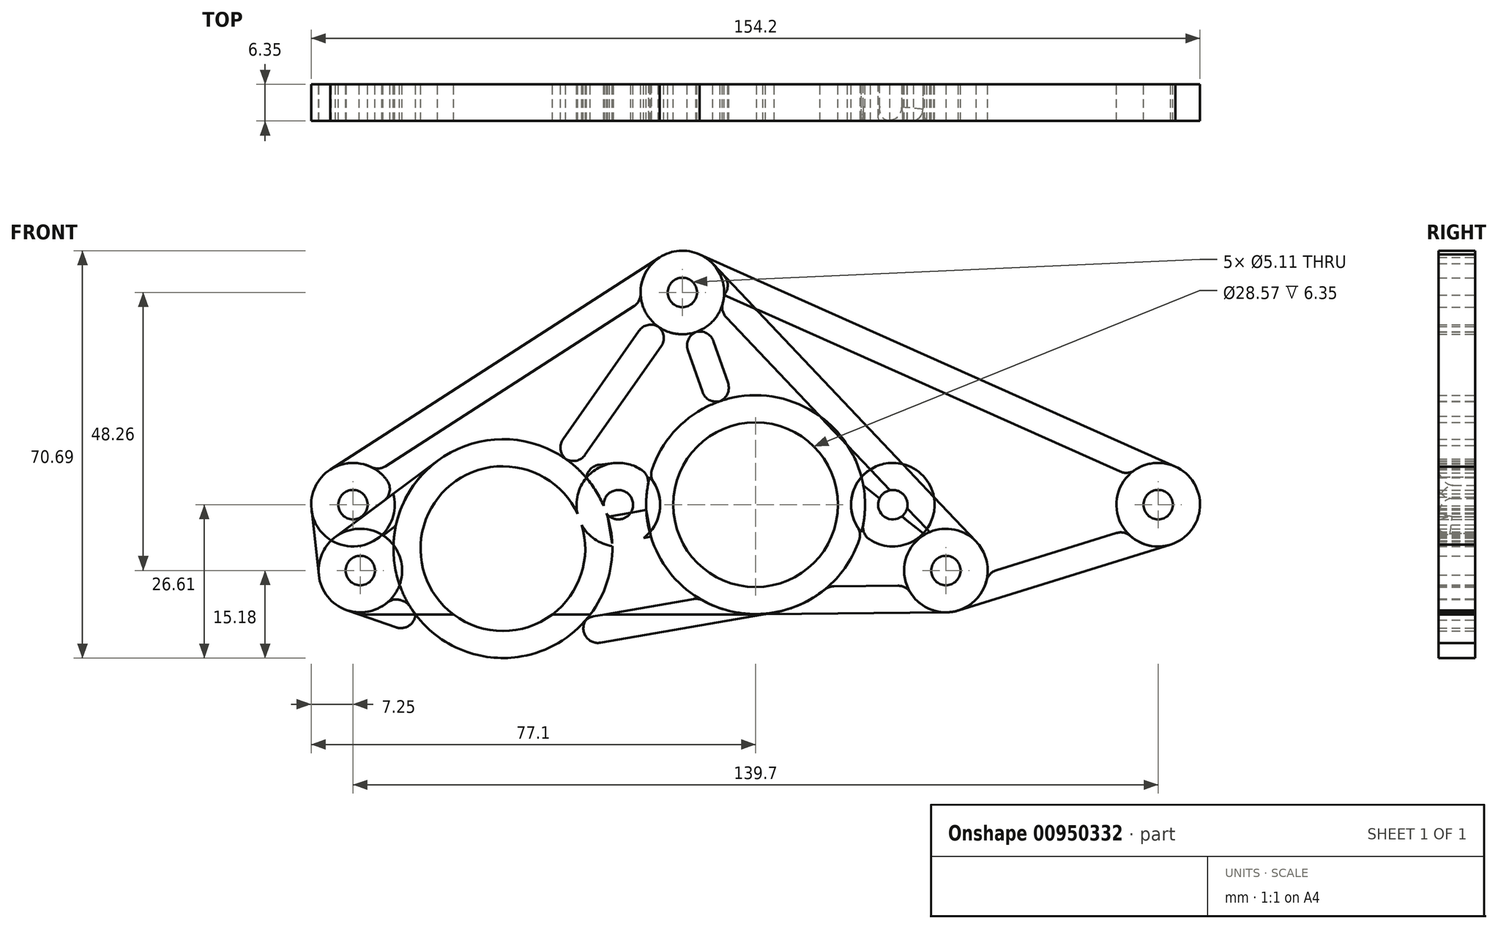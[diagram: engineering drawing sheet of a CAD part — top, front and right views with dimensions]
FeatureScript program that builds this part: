
annotation { "Feature Type Name" : "Feature", "Feature Type Description" : "" }
export const myFeature = defineFeature(function(context is Context, id is Id, definition is map)
    precondition{}
    {
        {
            var Q0;
            Q0=qCreatedBy(makeId("Front.planeOp"),FACE);
            var sketch = newSketch(context, id + "F0", { "sketchPlane" : qUnion([Q0])});
            skCircle(sketch, "E0", {"center": v(0, 0) * mm, "radius": 14.29 * mm});
            skCircle(sketch, "E1", {"center": v(-43.84, -7.62) * mm, "radius": 14.29 * mm});
            skCircle(sketch, "E2", {"center": v(-16.51, 54.1) * mm, "radius": 14.29 * mm, "construction": true});
            skCircle(sketch, "E3", {"center": v(18.98, 57.02) * mm, "radius": 6.35 * mm, "construction": true});
            skCircle(sketch, "E4", {"center": v(-50.18, 42.51) * mm, "radius": 6.35 * mm, "construction": true});
            skLineSegment(sketch, "E5.bottom", {"start": v(38.1, -19.05) * mm, "end": v(-76.2, -19.05) * mm});
            skLineSegment(sketch, "E5.top", {"start": v(38.1, 82.55) * mm, "end": v(-76.2, 82.55) * mm, "construction": true});
            skLineSegment(sketch, "E5.left", {"start": v(38.1, -19.05) * mm, "end": v(38.1, 82.55) * mm, "construction": true});
            skLineSegment(sketch, "E5.right", {"start": v(-76.2, -19.05) * mm, "end": v(-76.2, 82.55) * mm, "construction": true});
            skCircle(sketch, "E6", {"center": v(-68.58, -11.43) * mm, "radius": 2.55 * mm});
            skCircle(sketch, "E7", {"center": v(33.02, -11.43) * mm, "radius": 2.55 * mm});
            skCircle(sketch, "E8", {"center": v(-43.84, -7.62) * mm, "radius": 18.99 * mm});
            skCircle(sketch, "E9", {"center": v(0, 0) * mm, "radius": 18.99 * mm});
            skCircle(sketch, "E10", {"center": v(-12.7, 36.83) * mm, "radius": 2.55 * mm});
            skCircle(sketch, "E11", {"center": v(-12.7, 36.83) * mm, "radius": 7.25 * mm});
            skCircle(sketch, "E12", {"center": v(-68.58, -11.43) * mm, "radius": 7.25 * mm});
            skCircle(sketch, "E13", {"center": v(33.02, -11.43) * mm, "radius": 7.25 * mm});
            skLineSegment(sketch, "E14", {"start": v(11.88, 14.81) * mm, "end": v(37.56, -5.77) * mm, "construction": true});
            skLineSegment(sketch, "E15", {"start": v(0.18, -18.99) * mm, "end": v(33.09, -18.68) * mm});
            skLineSegment(sketch, "E16", {"start": v(18.7, 3.33) * mm, "end": v(29.32, -5.2) * mm});
            skLineSegment(sketch, "E17", {"start": v(12.64, -14.17) * mm, "end": v(26.26, -14.05) * mm});
            skLineSegment(sketch, "E18", {"start": v(-70.97, -18.28) * mm, "end": v(-50.09, -25.55) * mm});
            skLineSegment(sketch, "E19", {"start": v(-72.92, -5.62) * mm, "end": v(-55.2, 7.6) * mm});
            skLineSegment(sketch, "E20", {"start": v(-64.67, -5.33) * mm, "end": v(-62.4, -3.64) * mm});
            skLineSegment(sketch, "E21", {"start": v(-63, -16.07) * mm, "end": v(-60.35, -17) * mm});
            skLineSegment(sketch, "E22", {"start": v(-25.68, -2.08) * mm, "end": v(-18.96, -0.91) * mm});
            skLineSegment(sketch, "E23", {"start": v(-18.96, -0.91) * mm, "end": v(-18.16, -5.54) * mm});
            skLineSegment(sketch, "E24", {"start": v(-18.16, -5.54) * mm, "end": v(-24.88, -6.7) * mm});
            skLineSegment(sketch, "E25", {"start": v(-24.88, -6.7) * mm, "end": v(-25.68, -2.08) * mm});
            skLineSegment(sketch, "E26", {"start": v(-12.68, 29.58) * mm, "end": v(-8.36, 17.05) * mm});
            skLineSegment(sketch, "E27", {"start": v(-8.36, 17.05) * mm, "end": v(-3.92, 18.58) * mm, "construction": true});
            skLineSegment(sketch, "E28", {"start": v(-3.92, 18.58) * mm, "end": v(-8.24, 31.11) * mm});
            skLineSegment(sketch, "E29", {"start": v(-8.24, 31.11) * mm, "end": v(-12.68, 29.58) * mm, "construction": true});
            skLineSegment(sketch, "E30", {"start": v(-18.56, 32.56) * mm, "end": v(-34.96, 9.16) * mm});
            skLineSegment(sketch, "E31", {"start": v(-34.96, 9.16) * mm, "end": v(-31.1, 6.46) * mm, "construction": true});
            skLineSegment(sketch, "E32", {"start": v(-31.1, 6.46) * mm, "end": v(-14.71, 29.86) * mm});
            skLineSegment(sketch, "E33", {"start": v(-14.71, 29.86) * mm, "end": v(-18.56, 32.56) * mm, "construction": true});
            skCircle(sketch, "E34", {"center": v(0, 0) * mm, "radius": 23.81 * mm, "construction": true});
            skLineSegment(sketch, "E35", {"start": v(-7.44, 41.82) * mm, "end": v(38.28, -6.44) * mm});
            skLineSegment(sketch, "E36", {"start": v(-6.18, 33.66) * mm, "end": v(30.2, -4.75) * mm});
            skCircle(sketch, "E37", {"center": v(23.81, 0) * mm, "radius": 2.55 * mm});
            skCircle(sketch, "E38", {"center": v(23.81, 0) * mm, "radius": 7.25 * mm});
            skCircle(sketch, "E39", {"center": v(-23.81, 0) * mm, "radius": 2.55 * mm});
            skCircle(sketch, "E40", {"center": v(-23.81, 0) * mm, "radius": 7.25 * mm});
            skLineSegment(sketch, "E41", {"start": v(-69.85, 0) * mm, "end": v(69.85, 0) * mm, "construction": true});
            skCircle(sketch, "E42", {"center": v(69.85, 0) * mm, "radius": 2.55 * mm});
            skCircle(sketch, "E43", {"center": v(69.85, 0) * mm, "radius": 7.25 * mm});
            skCircle(sketch, "E44", {"center": v(-69.85, 0) * mm, "radius": 7.25 * mm});
            skCircle(sketch, "E45", {"center": v(-69.85, 0) * mm, "radius": 2.55 * mm});
            skLineSegment(sketch, "E46", {"start": v(-9.75, 43.45) * mm, "end": v(72.8, 6.62) * mm});
            skLineSegment(sketch, "E47", {"start": v(-5.46, 36.4) * mm, "end": v(64.7, 5.1) * mm});
            skLineSegment(sketch, "E48", {"start": v(64.12, -4.45) * mm, "end": v(40.26, -11.86) * mm});
            skLineSegment(sketch, "E49", {"start": v(72, -6.93) * mm, "end": v(35.17, -18.36) * mm});
            skLineSegment(sketch, "E50", {"start": v(-73.78, 6.1) * mm, "end": v(-16.63, 42.93) * mm});
            skLineSegment(sketch, "E51", {"start": v(-65.53, 5.82) * mm, "end": v(-19.79, 35.3) * mm});
            skLineSegment(sketch, "E52", {"start": v(-77.06, -0.8) * mm, "end": v(-75.79, -12.23) * mm});
            skLineSegment(sketch, "E53", {"start": v(-40.6, -26.33) * mm, "end": v(3.25, -18.7) * mm});
            skLineSegment(sketch, "E54", {"start": v(-29.08, -19.56) * mm, "end": v(-9.87, -16.22) * mm});
            skLineSegment(sketch, "E55", {"start": v(27.44, -6.28) * mm, "end": v(29.32, -5.2) * mm});
            skLineSegment(sketch, "E56", {"start": v(-31.1, 6.46) * mm, "end": v(-24.64, 7.2) * mm});
            skSolve(sketch);
        }
        {
            var Q0;
            Q0=makeQuery(id+"F0.imprint","IMPRINT",FACE,{"disambiguationData":[TD([[makeQuery(id+"F0.imprint","IMPRINT",EDGE,{"derivedFrom":sQuery(id+"F0.wireOp",EDGE,"E0")}),-1.0]])]});
            var Q1;
            {var subQ0=sQuery(id+"F0.wireOp",EDGE,"E5.bottom");var subQ1=sQuery(id+"F0.wireOp",EDGE,"E1");var subQ2=makeQuery(id+"F0.imprint","INTERSECT",VERTEX,{"disambiguationData":[OD(0.0)],"derivedFrom":[subQ1,subQ0]});Q1=makeQuery(id+"F0.imprint","IMPRINT",FACE,{"disambiguationData":[TD([[makeQuery(id+"F0.imprint","IMPRINT",EDGE,{"disambiguationData":[TD([[subQ2,-1.0]])],"derivedFrom":subQ1}),-1.0]])]});}
            var Q2;
            {var subQ0=sQuery(id+"F0.wireOp",EDGE,"E5.bottom");var subQ1=sQuery(id+"F0.wireOp",EDGE,"E1");var subQ2=makeQuery(id+"F0.imprint","INTERSECT",VERTEX,{"disambiguationData":[OD(0.0)],"derivedFrom":[subQ1,subQ0]});Q2=makeQuery(id+"F0.imprint","IMPRINT",FACE,{"disambiguationData":[TD([[makeQuery(id+"F0.imprint","IMPRINT",EDGE,{"disambiguationData":[TD([[subQ2,1.0]])],"derivedFrom":subQ1}),-1.0]])]});}
            var Q3;
            Q3=makeQuery(id+"F0.imprint","IMPRINT",FACE,{"disambiguationData":[TD([[makeQuery(id+"F0.imprint","IMPRINT",EDGE,{"derivedFrom":sQuery(id+"F0.wireOp",EDGE,"E7")}),-1.0]])]});
            var Q4;
            {var subQ0=sQuery(id+"F0.wireOp",EDGE,"E14");Q4=makeQuery(id+"F0.imprint","IMPRINT",FACE,{"disambiguationData":[TD([[makeQuery(id+"F0.imprint","IMPRINT",EDGE,{"derivedFrom":subQ0}),-1.0]])]});}
            var Q5;
            {var subQ0=sQuery(id+"F0.wireOp",EDGE,"E15");Q5=makeQuery(id+"F0.imprint","IMPRINT",FACE,{"disambiguationData":[TD([[makeQuery(id+"F0.imprint","IMPRINT",EDGE,{"derivedFrom":subQ0}),1.0]])]});}
            var Q6;
            {var subQ1=sQuery(id+"F0.wireOp",EDGE,"E22");Q6=makeQuery(id+"F0.imprint","IMPRINT",FACE,{"disambiguationData":[TD([[makeQuery(id+"F0.imprint","IMPRINT",EDGE,{"derivedFrom":subQ1}),-1.0]])]});}
            var Q7;
            {var subQ1=sQuery(id+"F0.wireOp",EDGE,"E26");Q7=makeQuery(id+"F0.imprint","IMPRINT",FACE,{"disambiguationData":[TD([[makeQuery(id+"F0.imprint","IMPRINT",EDGE,{"derivedFrom":subQ1}),1.0]])]});}
            var Q8;
            Q8=makeQuery(id+"F0.imprint","IMPRINT",FACE,{"disambiguationData":[TD([[makeQuery(id+"F0.imprint","IMPRINT",EDGE,{"derivedFrom":sQuery(id+"F0.wireOp",EDGE,"E10")}),-1.0]])]});
            var Q9;
            {var subQ1=sQuery(id+"F0.wireOp",EDGE,"E30");Q9=makeQuery(id+"F0.imprint","IMPRINT",FACE,{"disambiguationData":[TD([[makeQuery(id+"F0.imprint","IMPRINT",EDGE,{"derivedFrom":subQ1}),1.0]])]});}
            var Q10;
            {var subQ0=sQuery(id+"F0.wireOp",EDGE,"E33");Q10=makeQuery(id+"F0.imprint","IMPRINT",FACE,{"disambiguationData":[TD([[makeQuery(id+"F0.imprint","IMPRINT",EDGE,{"derivedFrom":subQ0}),1.0]])]});}
            var Q11;
            {var subQ0=sQuery(id+"F0.wireOp",EDGE,"E29");Q11=makeQuery(id+"F0.imprint","IMPRINT",FACE,{"disambiguationData":[TD([[makeQuery(id+"F0.imprint","IMPRINT",EDGE,{"derivedFrom":subQ0}),1.0]])]});}
            var Q12;
            {var subQ0=sQuery(id+"F0.wireOp",EDGE,"E27");Q12=makeQuery(id+"F0.imprint","IMPRINT",FACE,{"disambiguationData":[TD([[makeQuery(id+"F0.imprint","IMPRINT",EDGE,{"derivedFrom":subQ0}),1.0]])]});}
            var Q13;
            {var subQ0=sQuery(id+"F0.wireOp",EDGE,"E23");Q13=makeQuery(id+"F0.imprint","IMPRINT",FACE,{"disambiguationData":[TD([[makeQuery(id+"F0.imprint","IMPRINT",EDGE,{"derivedFrom":subQ0}),-1.0]])]});}
            var Q14;
            {var subQ0=sQuery(id+"F0.wireOp",EDGE,"E25");Q14=makeQuery(id+"F0.imprint","IMPRINT",FACE,{"disambiguationData":[TD([[makeQuery(id+"F0.imprint","IMPRINT",EDGE,{"derivedFrom":subQ0}),-1.0]])]});}
            var Q15;
            {var subQ5=sQuery(id+"F0.wireOp",EDGE,"E21");Q15=makeQuery(id+"F0.imprint","IMPRINT",FACE,{"disambiguationData":[TD([[makeQuery(id+"F0.imprint","IMPRINT",EDGE,{"derivedFrom":subQ5}),-1.0]])]});}
            var Q16;
            {var subQ0=sQuery(id+"F0.wireOp",EDGE,"E19");Q16=makeQuery(id+"F0.imprint","IMPRINT",FACE,{"disambiguationData":[TD([[makeQuery(id+"F0.imprint","IMPRINT",EDGE,{"derivedFrom":subQ0}),-1.0]])]});}
            var Q17;
            Q17=makeQuery(id+"F0.imprint","IMPRINT",FACE,{"disambiguationData":[TD([[makeQuery(id+"F0.imprint","IMPRINT",EDGE,{"derivedFrom":sQuery(id+"F0.wireOp",EDGE,"E6")}),-1.0]])]});
            var Q18;
            {var subQ0=sQuery(id+"F0.wireOp",EDGE,"E18");var subQ1=sQuery(id+"F0.wireOp",EDGE,"E5.bottom");var subQ2=makeQuery(id+"F0.imprint","INTERSECT",VERTEX,{"derivedFrom":[subQ1,subQ0]});Q18=makeQuery(id+"F0.imprint","IMPRINT",FACE,{"disambiguationData":[TD([[makeQuery(id+"F0.imprint","IMPRINT",EDGE,{"disambiguationData":[TD([[subQ2,1.0]])],"derivedFrom":subQ1}),1.0]])]});}
            var Q19;
            {var subQ0=sQuery(id+"F0.wireOp",EDGE,"E31");Q19=makeQuery(id+"F0.imprint","IMPRINT",FACE,{"disambiguationData":[TD([[makeQuery(id+"F0.imprint","IMPRINT",EDGE,{"derivedFrom":subQ0}),1.0]])]});}
            var Q20;
            {var subQ0=sQuery(id+"F0.wireOp",EDGE,"E13");var subQ1=sQuery(id+"F0.wireOp",EDGE,"E5.left");var subQ2=makeQuery(id+"F0.imprint","INTERSECT",VERTEX,{"disambiguationData":[OD(0.0)],"derivedFrom":[subQ1,subQ0]});Q20=makeQuery(id+"F0.imprint","IMPRINT",FACE,{"disambiguationData":[TD([[makeQuery(id+"F0.imprint","IMPRINT",EDGE,{"disambiguationData":[TD([[subQ2,-1.0]])],"derivedFrom":subQ1}),-1.0]])]});}
            var Q21;
            {var subQ5=sQuery(id+"F0.wireOp",EDGE,"E25");Q21=makeQuery(id+"F0.imprint","IMPRINT",FACE,{"disambiguationData":[TD([[makeQuery(id+"F0.imprint","IMPRINT",EDGE,{"derivedFrom":subQ5}),1.0]])]});}
            var Q22;
            {var subQ1=sQuery(id+"F0.wireOp",EDGE,"E9");var subQ3=sQuery(id+"F0.wireOp",EDGE,"E40");var subQ4=makeQuery(id+"F0.imprint","INTERSECT",VERTEX,{"disambiguationData":[OD(0.0)],"derivedFrom":[subQ1,subQ3]});Q22=makeQuery(id+"F0.imprint","IMPRINT",FACE,{"disambiguationData":[TD([[makeQuery(id+"F0.imprint","IMPRINT",EDGE,{"disambiguationData":[TD([[subQ4,1.0]])],"derivedFrom":subQ3}),1.0]])]});}
            var Q23;
            {var subQ0=sQuery(id+"F0.wireOp",EDGE,"E22");Q23=makeQuery(id+"F0.imprint","IMPRINT",FACE,{"disambiguationData":[TD([[makeQuery(id+"F0.imprint","IMPRINT",EDGE,{"derivedFrom":subQ0}),1.0]])]});}
            var Q24;
            {var subQ5=sQuery(id+"F0.wireOp",EDGE,"E36");var subQ7=sQuery(id+"F0.wireOp",EDGE,"E9");var subQ9=makeQuery(id+"F0.imprint","INTERSECT",VERTEX,{"disambiguationData":[OD(0.0)],"derivedFrom":[subQ7,subQ5]});Q24=makeQuery(id+"F0.imprint","IMPRINT",FACE,{"disambiguationData":[TD([[makeQuery(id+"F0.imprint","IMPRINT",EDGE,{"disambiguationData":[TD([[subQ9,-1.0]])],"derivedFrom":subQ7}),-1.0]])]});}
            var Q25;
            {var subQ0=sQuery(id+"F0.wireOp",EDGE,"E36");var subQ1=sQuery(id+"F0.wireOp",EDGE,"E9");var subQ2=makeQuery(id+"F0.imprint","INTERSECT",VERTEX,{"disambiguationData":[OD(0.0)],"derivedFrom":[subQ1,subQ0]});Q25=makeQuery(id+"F0.imprint","IMPRINT",FACE,{"disambiguationData":[TD([[makeQuery(id+"F0.imprint","IMPRINT",EDGE,{"disambiguationData":[TD([[subQ2,-1.0]])],"derivedFrom":subQ1}),1.0]])]});}
            var Q26;
            {var subQ0=sQuery(id+"F0.wireOp",EDGE,"E9");var subQ1=makeQuery(id+"F0.imprint","INTERSECT",VERTEX,{"derivedFrom":[subQ0,sQuery(id+"F0.wireOp",EDGE,"E16")]});Q26=makeQuery(id+"F0.imprint","IMPRINT",FACE,{"disambiguationData":[TD([[makeQuery(id+"F0.imprint","IMPRINT",EDGE,{"disambiguationData":[TD([[subQ1,-1.0]])],"derivedFrom":subQ0}),1.0]])]});}
            var Q27;
            {var subQ0=sQuery(id+"F0.wireOp",EDGE,"E37");var subQ1=sQuery(id+"F0.wireOp",EDGE,"E16");var subQ2=makeQuery(id+"F0.imprint","INTERSECT",VERTEX,{"disambiguationData":[OD(1.0)],"derivedFrom":[subQ1,subQ0]});Q27=makeQuery(id+"F0.imprint","IMPRINT",FACE,{"disambiguationData":[TD([[makeQuery(id+"F0.imprint","IMPRINT",EDGE,{"disambiguationData":[TD([[subQ2,-1.0]])],"derivedFrom":subQ1}),1.0]])]});}
            var Q28;
            {var subQ4=sQuery(id+"F0.wireOp",EDGE,"E38");var subQ7=sQuery(id+"F0.wireOp",EDGE,"E35");var subQ8=makeQuery(id+"F0.imprint","INTERSECT",VERTEX,{"disambiguationData":[OD(0.0)],"derivedFrom":[subQ7,subQ4]});Q28=makeQuery(id+"F0.imprint","IMPRINT",FACE,{"disambiguationData":[TD([[makeQuery(id+"F0.imprint","IMPRINT",EDGE,{"disambiguationData":[TD([[subQ8,-1.0]])],"derivedFrom":subQ7}),-1.0]])]});}
            var Q29;
            {var subQ0=sQuery(id+"F0.wireOp",EDGE,"E38");var subQ1=sQuery(id+"F0.wireOp",EDGE,"E35");var subQ2=makeQuery(id+"F0.imprint","INTERSECT",VERTEX,{"disambiguationData":[OD(0.0)],"derivedFrom":[subQ1,subQ0]});Q29=makeQuery(id+"F0.imprint","IMPRINT",FACE,{"disambiguationData":[TD([[makeQuery(id+"F0.imprint","IMPRINT",EDGE,{"disambiguationData":[TD([[subQ2,-1.0]])],"derivedFrom":subQ1}),1.0]])]});}
            var Q30;
            {var subQ0=sQuery(id+"F0.wireOp",EDGE,"E35");var subQ1=sQuery(id+"F0.wireOp",EDGE,"E13");var subQ2=makeQuery(id+"F0.imprint","INTERSECT",VERTEX,{"derivedFrom":[subQ1,subQ0]});Q30=makeQuery(id+"F0.imprint","IMPRINT",FACE,{"disambiguationData":[TD([[makeQuery(id+"F0.imprint","IMPRINT",EDGE,{"disambiguationData":[TD([[subQ2,-1.0]])],"derivedFrom":subQ1}),-1.0]])]});}
            var Q31;
            {var subQ0=sQuery(id+"F0.wireOp",EDGE,"E16");var subQ1=sQuery(id+"F0.wireOp",EDGE,"E13");var subQ2=makeQuery(id+"F0.imprint","INTERSECT",VERTEX,{"derivedFrom":[subQ1,subQ0]});Q31=makeQuery(id+"F0.imprint","IMPRINT",FACE,{"disambiguationData":[TD([[makeQuery(id+"F0.imprint","IMPRINT",EDGE,{"disambiguationData":[TD([[subQ2,1.0]])],"derivedFrom":subQ1}),-1.0]])]});}
            var Q32;
            {var subQ1=sQuery(id+"F0.wireOp",EDGE,"E16");var subQ7=sQuery(id+"F0.wireOp",EDGE,"E9");var subQ8=makeQuery(id+"F0.imprint","INTERSECT",VERTEX,{"derivedFrom":[subQ7,subQ1]});Q32=makeQuery(id+"F0.imprint","IMPRINT",FACE,{"disambiguationData":[TD([[makeQuery(id+"F0.imprint","IMPRINT",EDGE,{"disambiguationData":[TD([[subQ8,-1.0]])],"derivedFrom":subQ7}),-1.0]])]});}
            var Q33;
            {var subQ1=sQuery(id+"F0.wireOp",EDGE,"E16");var subQ6=sQuery(id+"F0.wireOp",EDGE,"E9");var subQ7=makeQuery(id+"F0.imprint","INTERSECT",VERTEX,{"derivedFrom":[subQ6,subQ1]});Q33=makeQuery(id+"F0.imprint","IMPRINT",FACE,{"disambiguationData":[TD([[makeQuery(id+"F0.imprint","IMPRINT",EDGE,{"disambiguationData":[TD([[subQ7,1.0]])],"derivedFrom":subQ6}),-1.0]])]});}
            var Q34;
            {var subQ0=sQuery(id+"F0.wireOp",EDGE,"E40");var subQ1=sQuery(id+"F0.wireOp",EDGE,"E1");var subQ2=makeQuery(id+"F0.imprint","INTERSECT",VERTEX,{"disambiguationData":[OD(1.0)],"derivedFrom":[subQ1,subQ0]});Q34=makeQuery(id+"F0.imprint","IMPRINT",FACE,{"disambiguationData":[TD([[makeQuery(id+"F0.imprint","IMPRINT",EDGE,{"disambiguationData":[TD([[subQ2,1.0]])],"derivedFrom":subQ1}),-1.0]])]});}
            var Q35;
            {var subQ0=sQuery(id+"F0.wireOp",EDGE,"E46");Q35=makeQuery(id+"F0.imprint","IMPRINT",FACE,{"disambiguationData":[TD([[makeQuery(id+"F0.imprint","IMPRINT",EDGE,{"derivedFrom":subQ0}),-1.0]])]});}
            var Q36;
            Q36=makeQuery(id+"F0.imprint","IMPRINT",FACE,{"disambiguationData":[TD([[makeQuery(id+"F0.imprint","IMPRINT",EDGE,{"derivedFrom":sQuery(id+"F0.wireOp",EDGE,"E42")}),-1.0]])]});
            var Q37;
            {var subQ0=sQuery(id+"F0.wireOp",EDGE,"E48");Q37=makeQuery(id+"F0.imprint","IMPRINT",FACE,{"disambiguationData":[TD([[makeQuery(id+"F0.imprint","IMPRINT",EDGE,{"derivedFrom":subQ0}),1.0]])]});}
            var Q38;
            {var subQ0=sQuery(id+"F0.wireOp",EDGE,"E35");var subQ1=sQuery(id+"F0.wireOp",EDGE,"E11");var subQ2=makeQuery(id+"F0.imprint","INTERSECT",VERTEX,{"derivedFrom":[subQ1,subQ0]});Q38=makeQuery(id+"F0.imprint","IMPRINT",FACE,{"disambiguationData":[TD([[makeQuery(id+"F0.imprint","IMPRINT",EDGE,{"disambiguationData":[TD([[subQ2,1.0]])],"derivedFrom":subQ1}),-1.0]])]});}
            var Q39;
            Q39=makeQuery(id+"F0.imprint","IMPRINT",FACE,{"disambiguationData":[TD([[makeQuery(id+"F0.imprint","IMPRINT",EDGE,{"derivedFrom":sQuery(id+"F0.wireOp",EDGE,"E45")}),-1.0]])]});
            var Q40;
            {var subQ0=sQuery(id+"F0.wireOp",EDGE,"E12");var subQ1=makeQuery(id+"F0.imprint","INTERSECT",VERTEX,{"derivedFrom":[subQ0,sQuery(id+"F0.wireOp",EDGE,"E19")]});Q40=makeQuery(id+"F0.imprint","IMPRINT",FACE,{"disambiguationData":[TD([[makeQuery(id+"F0.imprint","IMPRINT",EDGE,{"disambiguationData":[TD([[subQ1,1.0]])],"derivedFrom":subQ0}),1.0]])]});}
            var Q41;
            {var subQ0=sQuery(id+"F0.wireOp",EDGE,"E20");Q41=makeQuery(id+"F0.imprint","IMPRINT",FACE,{"disambiguationData":[TD([[makeQuery(id+"F0.imprint","IMPRINT",EDGE,{"derivedFrom":subQ0}),1.0]])]});}
            var Q42;
            {var subQ0=sQuery(id+"F0.wireOp",EDGE,"E50");Q42=makeQuery(id+"F0.imprint","IMPRINT",FACE,{"disambiguationData":[TD([[makeQuery(id+"F0.imprint","IMPRINT",EDGE,{"derivedFrom":subQ0}),-1.0]])]});}
            var Q43;
            {var subQ0=sQuery(id+"F0.wireOp",EDGE,"E53");var subQ1=sQuery(id+"F0.wireOp",EDGE,"E5.bottom");var subQ2=makeQuery(id+"F0.imprint","INTERSECT",VERTEX,{"derivedFrom":[subQ1,subQ0]});Q43=makeQuery(id+"F0.imprint","IMPRINT",FACE,{"disambiguationData":[TD([[makeQuery(id+"F0.imprint","IMPRINT",EDGE,{"disambiguationData":[TD([[subQ2,-1.0]])],"derivedFrom":subQ1}),1.0]])]});}
            var Q44;
            {var subQ3=sQuery(id+"F0.wireOp",EDGE,"E53");var subQ7=sQuery(id+"F0.wireOp",EDGE,"E5.bottom");var subQ8=makeQuery(id+"F0.imprint","INTERSECT",VERTEX,{"derivedFrom":[subQ7,subQ3]});Q44=makeQuery(id+"F0.imprint","IMPRINT",FACE,{"disambiguationData":[TD([[makeQuery(id+"F0.imprint","IMPRINT",EDGE,{"disambiguationData":[TD([[subQ8,-1.0]])],"derivedFrom":subQ7}),-1.0]])]});}
            var Q45;
            {var subQ0=sQuery(id+"F0.wireOp",EDGE,"E17");Q45=makeQuery(id+"F0.imprint","IMPRINT",FACE,{"disambiguationData":[TD([[makeQuery(id+"F0.imprint","IMPRINT",EDGE,{"derivedFrom":subQ0}),-1.0]])]});}
            var Q46;
            {var subQ0=sQuery(id+"F0.wireOp",EDGE,"E52");Q46=makeQuery(id+"F0.imprint","IMPRINT",FACE,{"disambiguationData":[TD([[makeQuery(id+"F0.imprint","IMPRINT",EDGE,{"derivedFrom":subQ0}),1.0]])]});}
            var Q47;
            {var subQ0=sQuery(id+"F0.wireOp",EDGE,"E55");Q47=makeQuery(id+"F0.imprint","IMPRINT",FACE,{"disambiguationData":[TD([[makeQuery(id+"F0.imprint","IMPRINT",EDGE,{"derivedFrom":subQ0}),1.0]])]});}
            var Q48;
            {var subQ0=sQuery(id+"F0.wireOp",EDGE,"E56");Q48=makeQuery(id+"F0.imprint","IMPRINT",FACE,{"disambiguationData":[TD([[makeQuery(id+"F0.imprint","IMPRINT",EDGE,{"derivedFrom":subQ0}),-1.0]])]});}
            var Q49;
            {var subQ0=sQuery(id+"F0.wireOp",EDGE,"E38");var subQ1=sQuery(id+"F0.wireOp",EDGE,"E9");var subQ2=makeQuery(id+"F0.imprint","INTERSECT",VERTEX,{"disambiguationData":[OD(0.0)],"derivedFrom":[subQ1,subQ0]});Q49=makeQuery(id+"F0.imprint","IMPRINT",FACE,{"disambiguationData":[TD([[makeQuery(id+"F0.imprint","IMPRINT",EDGE,{"disambiguationData":[TD([[subQ2,-1.0]])],"derivedFrom":subQ1}),-1.0]])]});}
            var Q50;
            {var subQ0=sQuery(id+"F0.wireOp",EDGE,"E12");var subQ1=sQuery(id+"F0.wireOp",EDGE,"E8");var subQ2=makeQuery(id+"F0.imprint","INTERSECT",VERTEX,{"disambiguationData":[OD(0.0)],"derivedFrom":[subQ1,subQ0]});Q50=makeQuery(id+"F0.imprint","IMPRINT",FACE,{"disambiguationData":[TD([[makeQuery(id+"F0.imprint","IMPRINT",EDGE,{"disambiguationData":[TD([[subQ2,-1.0]])],"derivedFrom":subQ1}),1.0]])]});}
            var Q51;
            {var subQ0=sQuery(id+"F0.wireOp",EDGE,"E39");var subQ1=sQuery(id+"F0.wireOp",EDGE,"E8");var subQ2=makeQuery(id+"F0.imprint","INTERSECT",VERTEX,{"disambiguationData":[OD(1.0)],"derivedFrom":[subQ1,subQ0]});Q51=makeQuery(id+"F0.imprint","IMPRINT",FACE,{"disambiguationData":[TD([[makeQuery(id+"F0.imprint","IMPRINT",EDGE,{"disambiguationData":[TD([[subQ2,-1.0]])],"derivedFrom":subQ1}),-1.0]])]});}
            var Q52;
            {var subQ1=sQuery(id+"F0.wireOp",EDGE,"E9");var subQ3=sQuery(id+"F0.wireOp",EDGE,"E40");var subQ4=makeQuery(id+"F0.imprint","INTERSECT",VERTEX,{"disambiguationData":[OD(1.0)],"derivedFrom":[subQ1,subQ3]});Q52=makeQuery(id+"F0.imprint","IMPRINT",FACE,{"disambiguationData":[TD([[makeQuery(id+"F0.imprint","IMPRINT",EDGE,{"disambiguationData":[TD([[subQ4,1.0]])],"derivedFrom":subQ3}),-1.0]])]});}
            extrude(context, id + "F1", {"entities" : qUnion([Q0, Q1, Q2, Q3, Q4, Q5, Q6, Q7, Q8, Q9, Q10, Q11, Q12, Q13, Q14, Q15, Q16, Q17, Q18, Q19, Q20, Q21, Q22, Q23, Q24, Q25, Q26, Q27, Q28, Q29, Q30, Q31, Q32, Q33, Q34, Q35, Q36, Q37, Q38, Q39, Q40, Q41, Q42, Q43, Q44, Q45, Q46, Q47, Q48, Q49, Q50, Q51, Q52]), "depth" : 6.35 * mm, "offsetDistance" : 25.4 * mm});
        }
        {
            var Q0;
            Q0=makeQuery(id+"F1.opExtrude","SWEPT_EDGE",EDGE,{"disambiguationData":[OSD([sQuery(id+"F0.wireOp",EDGE,"E12"),sQuery(id+"F0.wireOp",EDGE,"E20")])]});
            var Q1;
            Q1=makeQuery(id+"F1.opExtrude","SWEPT_EDGE",EDGE,{"disambiguationData":[OSD([sQuery(id+"F0.wireOp",EDGE,"E12"),sQuery(id+"F0.wireOp",EDGE,"E21")])]});
            var Q2;
            Q2=makeQuery(id+"F1.opExtrude","SWEPT_EDGE",EDGE,{"disambiguationData":[OSD([sQuery(id+"F0.wireOp",EDGE,"E8"),sQuery(id+"F0.wireOp",EDGE,"E21")])]});
            var Q3;
            Q3=makeQuery(id+"F1.opExtrude","SWEPT_EDGE",EDGE,{"disambiguationData":[OSD([sQuery(id+"F0.wireOp",EDGE,"E44"),sQuery(id+"F0.wireOp",EDGE,"E51")])]});
            var Q4;
            Q4=makeQuery(id+"F1.opExtrude","SWEPT_EDGE",EDGE,{"disambiguationData":[OSD([sQuery(id+"F0.wireOp",EDGE,"E19"),sQuery(id+"F0.wireOp",EDGE,"E44")])]});
            var Q5;
            Q5=makeQuery(id+"F1.opExtrude","SWEPT_EDGE",EDGE,{"disambiguationData":[OSD([sQuery(id+"F0.wireOp",EDGE,"E8"),sQuery(id+"F0.wireOp",EDGE,"E30")])]});
            var Q6;
            Q6=makeQuery(id+"F1.opExtrude","SWEPT_EDGE",EDGE,{"disambiguationData":[OSD([sQuery(id+"F0.wireOp",EDGE,"E11"),sQuery(id+"F0.wireOp",EDGE,"E51")])]});
            var Q7;
            Q7=makeQuery(id+"F1.opExtrude","SWEPT_EDGE",EDGE,{"disambiguationData":[OSD([sQuery(id+"F0.wireOp",EDGE,"E11"),sQuery(id+"F0.wireOp",EDGE,"E30")])]});
            var Q8;
            Q8=makeQuery(id+"F1.opExtrude","SWEPT_EDGE",EDGE,{"disambiguationData":[OSD([sQuery(id+"F0.wireOp",EDGE,"E11"),sQuery(id+"F0.wireOp",EDGE,"E32")])]});
            var Q9;
            Q9=makeQuery(id+"F1.opExtrude","SWEPT_EDGE",EDGE,{"disambiguationData":[OSD([sQuery(id+"F0.wireOp",EDGE,"E11"),sQuery(id+"F0.wireOp",EDGE,"E26")])]});
            var Q10;
            {var subQ0=sQuery(id+"F0.wireOp",EDGE,"E40");var subQ1=sQuery(id+"F0.wireOp",EDGE,"E9");Q10=makeQuery(id+"F1.opExtrude","SWEPT_EDGE",EDGE,{"disambiguationData":[OSD([subQ1,subQ0]),TDD([makeQuery(id+"F0.imprint","INTERSECT",VERTEX,{"disambiguationData":[OD(0.0)],"derivedFrom":[subQ1,subQ0]})])]});}
            var Q11;
            Q11=makeQuery(id+"F1.opExtrude","SWEPT_EDGE",EDGE,{"disambiguationData":[OSD([sQuery(id+"F0.wireOp",EDGE,"E9"),sQuery(id+"F0.wireOp",EDGE,"E26")])]});
            var Q12;
            Q12=makeQuery(id+"F1.opExtrude","SWEPT_EDGE",EDGE,{"disambiguationData":[OSD([sQuery(id+"F0.wireOp",EDGE,"E9"),sQuery(id+"F0.wireOp",EDGE,"E28")])]});
            var Q13;
            Q13=makeQuery(id+"F1.opExtrude","SWEPT_EDGE",EDGE,{"disambiguationData":[OSD([sQuery(id+"F0.wireOp",EDGE,"E8"),sQuery(id+"F0.wireOp",EDGE,"E54")])]});
            var Q14;
            Q14=makeQuery(id+"F1.opExtrude","SWEPT_EDGE",EDGE,{"disambiguationData":[OSD([sQuery(id+"F0.wireOp",EDGE,"E9"),sQuery(id+"F0.wireOp",EDGE,"E54")])]});
            var Q15;
            {var subQ0=sQuery(id+"F0.wireOp",EDGE,"E38");var subQ1=sQuery(id+"F0.wireOp",EDGE,"E9");Q15=makeQuery(id+"F1.opExtrude","SWEPT_EDGE",EDGE,{"disambiguationData":[OSD([subQ1,subQ0]),TDD([makeQuery(id+"F0.imprint","INTERSECT",VERTEX,{"disambiguationData":[OD(1.0)],"derivedFrom":[subQ1,subQ0]})])]});}
            var Q16;
            Q16=makeQuery(id+"F1.opExtrude","SWEPT_EDGE",EDGE,{"disambiguationData":[OSD([sQuery(id+"F0.wireOp",EDGE,"E9"),sQuery(id+"F0.wireOp",EDGE,"E17")])]});
            var Q17;
            Q17=makeQuery(id+"F1.opExtrude","SWEPT_EDGE",EDGE,{"disambiguationData":[OSD([sQuery(id+"F0.wireOp",EDGE,"E13"),sQuery(id+"F0.wireOp",EDGE,"E48")])]});
            var Q18;
            Q18=makeQuery(id+"F1.opExtrude","SWEPT_EDGE",EDGE,{"disambiguationData":[OSD([sQuery(id+"F0.wireOp",EDGE,"E35"),sQuery(id+"F0.wireOp",EDGE,"E47")])]});
            var Q19;
            Q19=makeQuery(id+"F1.opExtrude","SWEPT_EDGE",EDGE,{"disambiguationData":[OSD([sQuery(id+"F0.wireOp",EDGE,"E11"),sQuery(id+"F0.wireOp",EDGE,"E28")])]});
            var Q20;
            Q20=makeQuery(id+"F1.opExtrude","SWEPT_EDGE",EDGE,{"disambiguationData":[OSD([sQuery(id+"F0.wireOp",EDGE,"E11"),sQuery(id+"F0.wireOp",EDGE,"E36")])]});
            var Q21;
            {var subQ0=sQuery(id+"F0.wireOp",EDGE,"E36");var subQ1=sQuery(id+"F0.wireOp",EDGE,"E9");Q21=makeQuery(id+"F1.opExtrude","SWEPT_EDGE",EDGE,{"disambiguationData":[OSD([subQ1,subQ0]),TDD([makeQuery(id+"F0.imprint","INTERSECT",VERTEX,{"disambiguationData":[OD(1.0)],"derivedFrom":[subQ1,subQ0]})])]});}
            var Q22;
            Q22=makeQuery(id+"F1.opExtrude","SWEPT_EDGE",EDGE,{"disambiguationData":[OSD([sQuery(id+"F0.wireOp",EDGE,"E13"),sQuery(id+"F0.wireOp",EDGE,"E17")])]});
            var Q23;
            Q23=makeQuery(id+"F1.opExtrude","SWEPT_EDGE",EDGE,{"disambiguationData":[OSD([sQuery(id+"F0.wireOp",EDGE,"E43"),sQuery(id+"F0.wireOp",EDGE,"E47")])]});
            var Q24;
            Q24=makeQuery(id+"F1.opExtrude","SWEPT_EDGE",EDGE,{"disambiguationData":[OSD([sQuery(id+"F0.wireOp",EDGE,"E43"),sQuery(id+"F0.wireOp",EDGE,"E48")])]});
            var Q25;
            {var subQ0=sQuery(id+"F0.wireOp",EDGE,"E40");var subQ1=sQuery(id+"F0.wireOp",EDGE,"E9");Q25=makeQuery(id+"F1.opExtrude","SWEPT_EDGE",EDGE,{"disambiguationData":[OSD([subQ1,subQ0]),TDD([makeQuery(id+"F0.imprint","INTERSECT",VERTEX,{"disambiguationData":[OD(1.0)],"derivedFrom":[subQ1,subQ0]})])]});}
            var Q26;
            Q26=makeQuery(id+"F1.opExtrude","CAP_EDGE",EDGE,{"disambiguationData":[OSD([sQuery(id+"F0.wireOp",EDGE,"E16")])],"isStart":false});
            var Q27;
            Q27=makeQuery(id+"F1.opExtrude","SWEPT_EDGE",EDGE,{"disambiguationData":[OSD([sQuery(id+"F0.wireOp",EDGE,"E13"),sQuery(id+"F0.wireOp",EDGE,"E16"),sQuery(id+"F0.wireOp",EDGE,"E55")])]});
            var Q28;
            Q28=makeQuery(id+"F1.opExtrude","SWEPT_EDGE",EDGE,{"disambiguationData":[OSD([sQuery(id+"F0.wireOp",EDGE,"E8"),sQuery(id+"F0.wireOp",EDGE,"E18")])]});
            var Q29;
            Q29=makeQuery(id+"F1.opExtrude","SWEPT_EDGE",EDGE,{"disambiguationData":[OSD([sQuery(id+"F0.wireOp",EDGE,"E8"),sQuery(id+"F0.wireOp",EDGE,"E19")])]});
            var Q30;
            Q30=makeQuery(id+"F1.opExtrude","SWEPT_EDGE",EDGE,{"disambiguationData":[OSD([sQuery(id+"F0.wireOp",EDGE,"E8"),sQuery(id+"F0.wireOp",EDGE,"E20")])]});
            var Q31;
            Q31=makeQuery(id+"F1.opExtrude","SWEPT_EDGE",EDGE,{"disambiguationData":[OSD([sQuery(id+"F0.wireOp",EDGE,"E8"),sQuery(id+"F0.wireOp",EDGE,"E21")])]});
            var Q32;
            Q32=makeQuery(id+"F1.opExtrude","SWEPT_EDGE",EDGE,{"disambiguationData":[OSD([sQuery(id+"F0.wireOp",EDGE,"E8"),sQuery(id+"F0.wireOp",EDGE,"E30")])]});
            var Q33;
            Q33=makeQuery(id+"F1.opExtrude","SWEPT_EDGE",EDGE,{"disambiguationData":[OSD([sQuery(id+"F0.wireOp",EDGE,"E8"),sQuery(id+"F0.wireOp",EDGE,"E53")])]});
            var Q34;
            Q34=makeQuery(id+"F1.opExtrude","SWEPT_EDGE",EDGE,{"disambiguationData":[OSD([sQuery(id+"F0.wireOp",EDGE,"E8"),sQuery(id+"F0.wireOp",EDGE,"E54")])]});
            var Q35;
            {var subQ0=sQuery(id+"F0.wireOp",EDGE,"E40");var subQ1=sQuery(id+"F0.wireOp",EDGE,"E9");Q35=makeQuery(id+"F1.opExtrude","SWEPT_EDGE",EDGE,{"disambiguationData":[OSD([subQ1,subQ0]),TDD([makeQuery(id+"F0.imprint","INTERSECT",VERTEX,{"disambiguationData":[OD(0.0)],"derivedFrom":[subQ1,subQ0]})])]});}
            var Q36;
            {var subQ0=sQuery(id+"F0.wireOp",EDGE,"E40");var subQ1=sQuery(id+"F0.wireOp",EDGE,"E9");Q36=makeQuery(id+"F1.opExtrude","SWEPT_EDGE",EDGE,{"disambiguationData":[OSD([subQ1,subQ0]),TDD([makeQuery(id+"F0.imprint","INTERSECT",VERTEX,{"disambiguationData":[OD(1.0)],"derivedFrom":[subQ1,subQ0]})])]});}
            var Q37;
            Q37=makeQuery(id+"F1.opExtrude","SWEPT_EDGE",EDGE,{"disambiguationData":[OSD([sQuery(id+"F0.wireOp",EDGE,"E8"),sQuery(id+"F0.wireOp",EDGE,"E24"),sQuery(id+"F0.wireOp",EDGE,"E25")])]});
            var Q38;
            Q38=makeQuery(id+"F1.opExtrude","SWEPT_EDGE",EDGE,{"disambiguationData":[OSD([sQuery(id+"F0.wireOp",EDGE,"E8"),sQuery(id+"F0.wireOp",EDGE,"E32"),sQuery(id+"F0.wireOp",EDGE,"E56")])]});
            fillet(context, id + "F2", {"entities" : qUnion([Q0, Q1, Q2, Q3, Q4, Q5, Q6, Q7, Q8, Q9, Q10, Q11, Q12, Q13, Q14, Q15, Q16, Q17, Q18, Q19, Q20, Q21, Q22, Q23, Q24, Q25, Q26, Q27, Q28, Q29, Q30, Q31, Q32, Q33, Q34, Q35, Q36, Q37, Q38]), "tangentPropagation" : true, "radius" : 2.54 * mm, "defaultsChanged" : false, "vertexSettings" : [], "allowEdgeOverflow" : false});
        }
        {
            var Q0;
            Q0=makeQuery(id+"F1.opExtrude","SWEPT_EDGE",EDGE,{"disambiguationData":[OSD([sQuery(id+"F0.wireOp",EDGE,"E8"),sQuery(id+"F0.wireOp",EDGE,"E20")])]});
            fillet(context, id + "F3", {"entities" : qUnion([Q0]), "tangentPropagation" : true, "radius" : 1.27 * mm, "defaultsChanged" : true, "vertexSettings" : [], "allowEdgeOverflow" : false});
        }
    });
